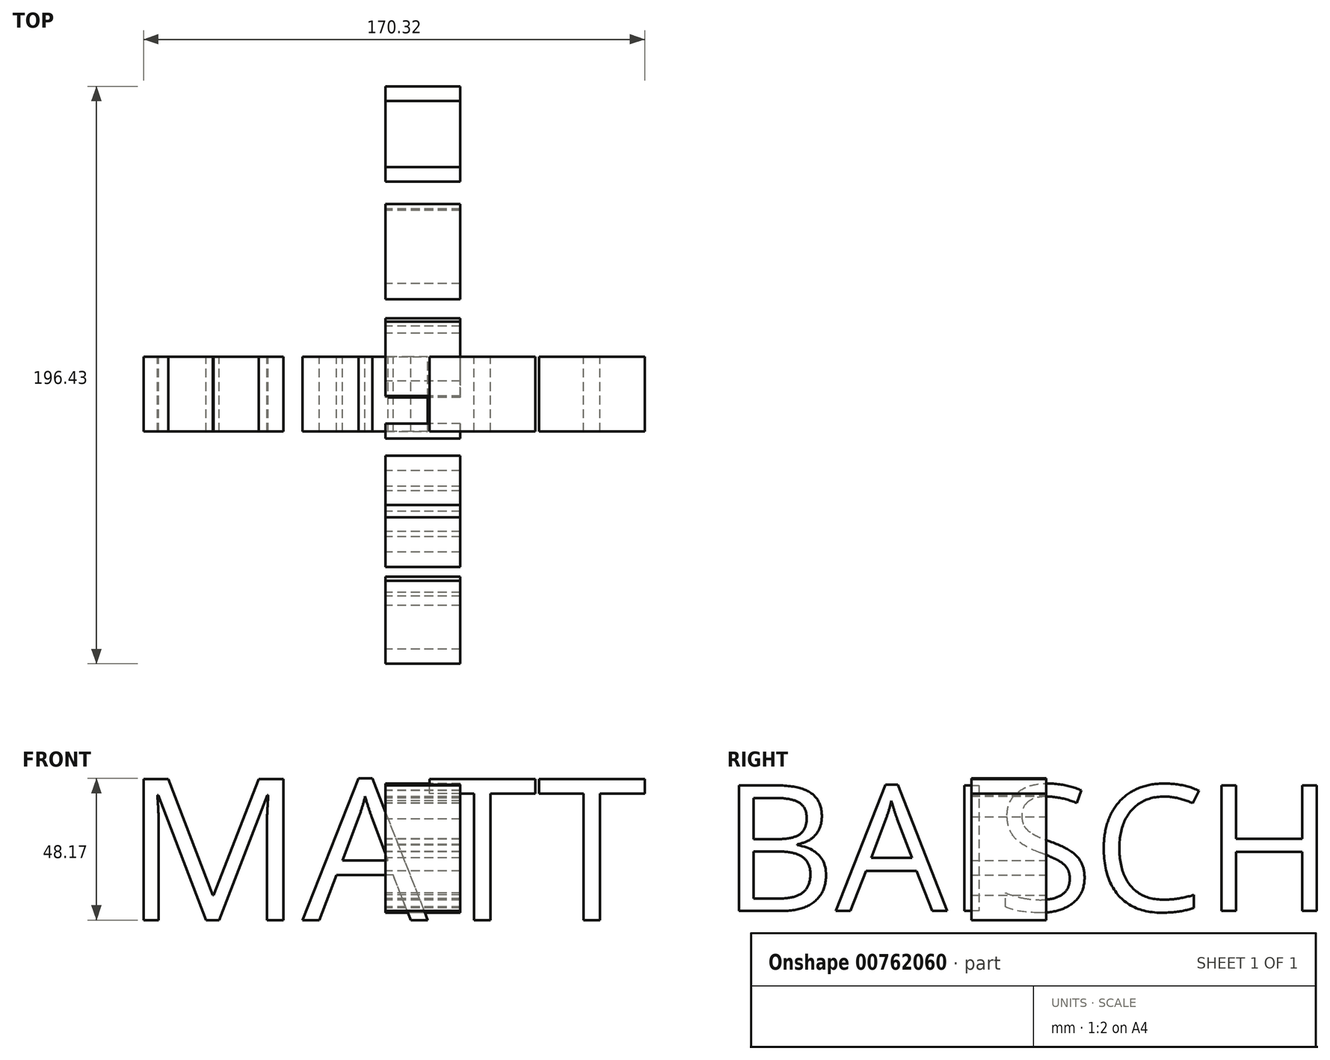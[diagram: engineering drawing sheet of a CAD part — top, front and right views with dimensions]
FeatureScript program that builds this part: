
annotation { "Feature Type Name" : "Feature", "Feature Type Description" : "" }
export const myFeature = defineFeature(function(context is Context, id is Id, definition is map)
    precondition{}
    {
        {
            var Q0;
            Q0=qCreatedBy(makeId("Front.planeOp"),FACE);
            var sketch = newSketch(context, id + "F0", { "sketchPlane" : qUnion([Q0])});
            skText(sketch, "E0", { "text": "MATT", "fontName": "OpenSans-Regular.ttf"});
            const initialGuessF0  = {"E0": [-0.08885, -0.02403, 1, 0, 0.04838]};
            skSetInitialGuess(sketch, initialGuessF0);
            skSolve(sketch);
        }
        {
            var Q0;
            Q0=qCreatedBy(makeId("Right.planeOp"),FACE);
            var sketch = newSketch(context, id + "F1", { "sketchPlane" : qUnion([Q0])});
            skText(sketch, "E1", { "text": "BAISCH", "fontName": "OpenSans-Regular.ttf"});
            const initialGuessF1  = {"E1": [-0.11025, -0.02093, 1, 0, 0.0431]};
            skSetInitialGuess(sketch, initialGuessF1);
            skSolve(sketch);
        }
        {
            var Q0;
            Q0=makeQuery(id+"F1.imprint","IMPRINT",FACE,{"disambiguationData":[TD([[makeQuery(id+"F1.imprint","IMPRINT",EDGE,{"derivedFrom":sQuery(id+"F1.wireOp",EDGE,"E1.sketch_text.stroke-38")}),-1.0]])]});
            var Q1;
            Q1=makeQuery(id+"F1.imprint","IMPRINT",FACE,{"disambiguationData":[TD([[makeQuery(id+"F1.imprint","IMPRINT",EDGE,{"derivedFrom":sQuery(id+"F1.wireOp",EDGE,"E1.sketch_text.stroke-42")}),-1.0]])]});
            var Q2;
            Q2=makeQuery(id+"F1.imprint","IMPRINT",FACE,{"disambiguationData":[TD([[makeQuery(id+"F1.imprint","IMPRINT",EDGE,{"derivedFrom":sQuery(id+"F1.wireOp",EDGE,"E1.sketch_text.stroke-67")}),-1.0]])]});
            var Q3;
            Q3=makeQuery(id+"F1.imprint","IMPRINT",FACE,{"disambiguationData":[TD([[makeQuery(id+"F1.imprint","IMPRINT",EDGE,{"derivedFrom":sQuery(id+"F1.wireOp",EDGE,"E1.sketch_text.stroke-82")}),-1.0]])]});
            var Q4;
            Q4=makeQuery(id+"F1.imprint","IMPRINT",FACE,{"disambiguationData":[TD([[makeQuery(id+"F1.imprint","IMPRINT",EDGE,{"derivedFrom":sQuery(id+"F1.wireOp",EDGE,"E1.sketch_text.stroke-25")}),-1.0]])]});
            var Q5;
            Q5=makeQuery(id+"F1.imprint","IMPRINT",FACE,{"disambiguationData":[TD([[makeQuery(id+"F1.imprint","IMPRINT",EDGE,{"derivedFrom":sQuery(id+"F1.wireOp",EDGE,"E1.sketch_text.stroke-0")}),-1.0]])]});
            extrude(context, id + "F2", {"entities" : qUnion([Q0, Q1, Q2, Q3, Q4, Q5]), "depth" : 25.4 * mm, "offsetDistance" : 25.4 * mm});
        }
        {
            var Q0;
            Q0 = qSketchRegion(id + "F0", true);
            extrude(context, id + "F3", {"entities" : qUnion([Q0]), "depth" : 25.4 * mm, "offsetDistance" : 25.4 * mm});
        }
    });
